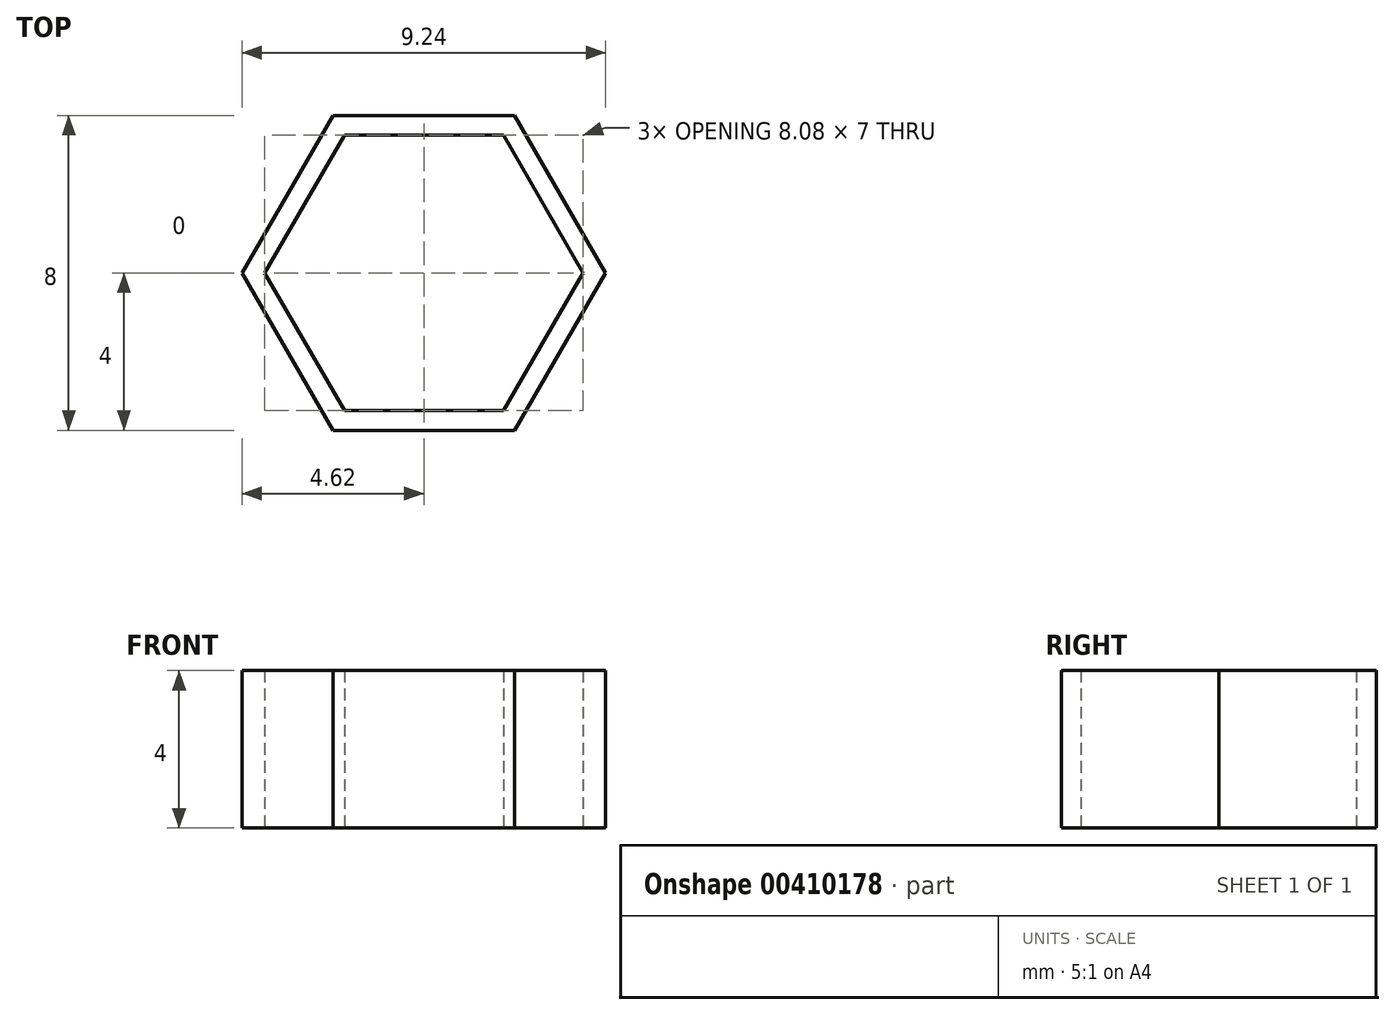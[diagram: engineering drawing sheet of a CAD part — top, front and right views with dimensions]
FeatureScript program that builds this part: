
annotation { "Feature Type Name" : "Feature", "Feature Type Description" : "" }
export const myFeature = defineFeature(function(context is Context, id is Id, definition is map)
    precondition{}
    {
        {
            var Q0;
            Q0=qCreatedBy(makeId("Top.planeOp"),FACE);
            var sketch = newSketch(context, id + "F0", { "sketchPlane" : qUnion([Q0])});
            skCircle(sketch, "E0.cCircle", {"center": v(0, 0) * mm, "radius": 3.5 * mm, "construction": true});
            skLineSegment(sketch, "E0.0", {"start": v(2.02, 3.5) * mm, "end": v(4.04, 0) * mm});
            skLineSegment(sketch, "E0.1", {"start": v(4.04, 0) * mm, "end": v(2.02, -3.5) * mm});
            skLineSegment(sketch, "E0.2", {"start": v(2.02, -3.5) * mm, "end": v(-2.02, -3.5) * mm});
            skLineSegment(sketch, "E0.3", {"start": v(-2.02, -3.5) * mm, "end": v(-4.04, 0) * mm});
            skLineSegment(sketch, "E0.4", {"start": v(-4.04, 0) * mm, "end": v(-2.02, 3.5) * mm});
            skLineSegment(sketch, "E0.5", {"start": v(-2.02, 3.5) * mm, "end": v(2.02, 3.5) * mm});
            skPoint(sketch, "E0.0.midPoint", {"position": v(3.03, 1.75) * mm});
            skCircle(sketch, "E1.cCircle", {"center": v(0, 0) * mm, "radius": 4 * mm, "construction": true});
            skLineSegment(sketch, "E1.0", {"start": v(2.3, 4) * mm, "end": v(4.62, 0) * mm});
            skLineSegment(sketch, "E1.1", {"start": v(4.62, 0) * mm, "end": v(2.3, -4) * mm});
            skLineSegment(sketch, "E1.2", {"start": v(2.3, -4) * mm, "end": v(-2.3, -4) * mm});
            skLineSegment(sketch, "E1.3", {"start": v(-2.3, -4) * mm, "end": v(-4.62, 0) * mm});
            skLineSegment(sketch, "E1.4", {"start": v(-4.62, 0) * mm, "end": v(-2.3, 4) * mm});
            skLineSegment(sketch, "E1.5", {"start": v(-2.3, 4) * mm, "end": v(2.3, 4) * mm});
            skPoint(sketch, "E1.0.midPoint", {"position": v(3.46, 2) * mm});
            skSolve(sketch);
        }
        {
            var Q0;
            Q0 = qSketchRegion(id + "F0", true);
            extrude(context, id + "F1", {"entities" : qUnion([Q0]), "depth" : 4 * mm});
        }
    });
